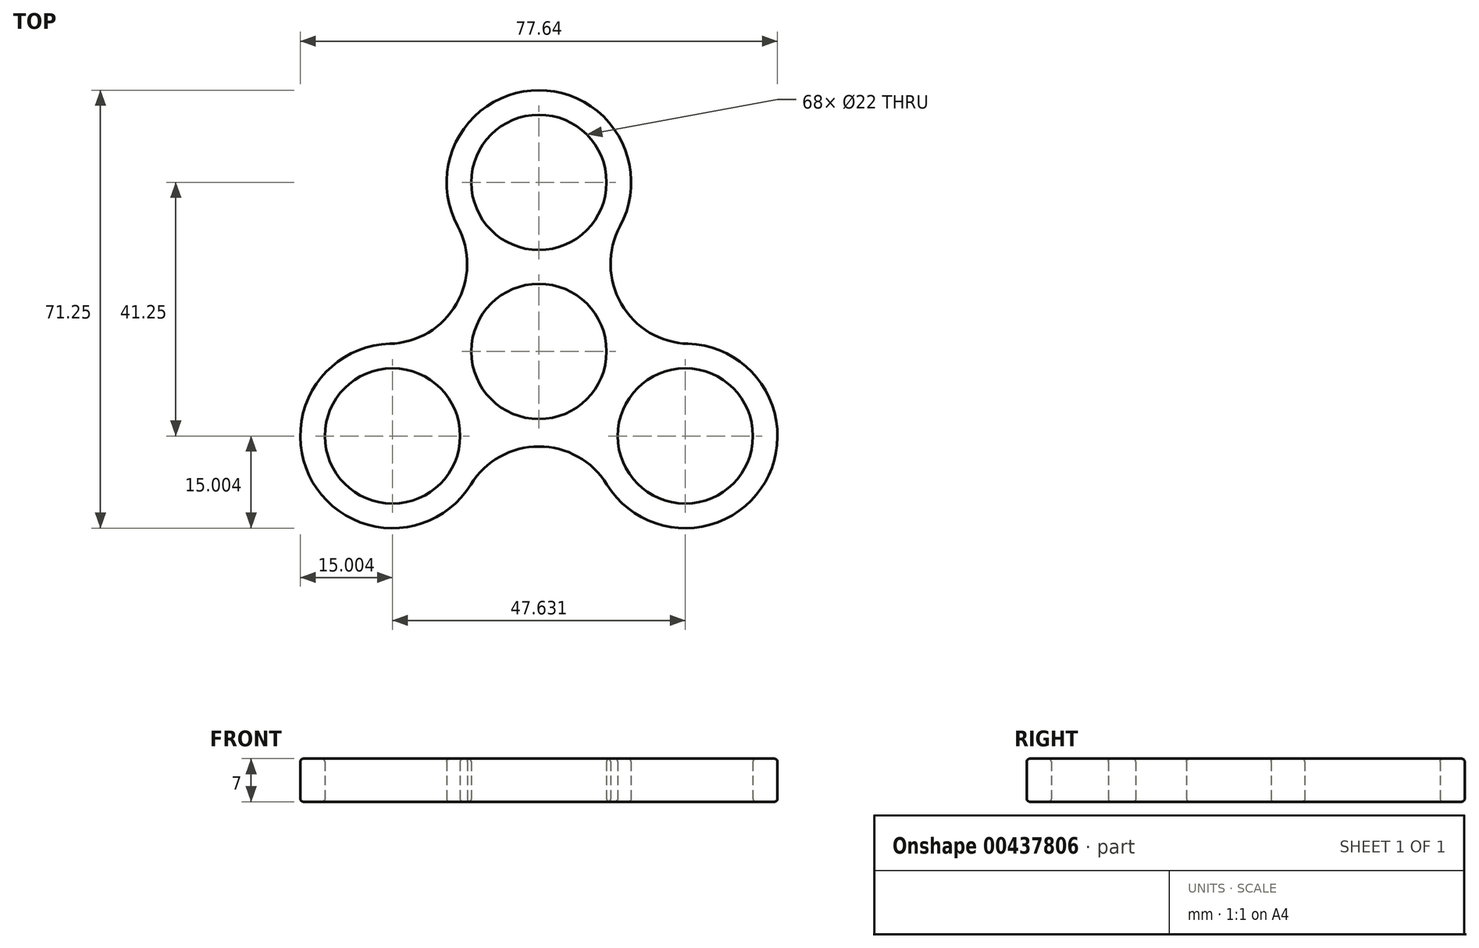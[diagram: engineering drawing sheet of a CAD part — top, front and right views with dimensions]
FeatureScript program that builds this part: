
annotation { "Feature Type Name" : "Feature", "Feature Type Description" : "" }
export const myFeature = defineFeature(function(context is Context, id is Id, definition is map)
    precondition{}
    {
        {
            var Q0;
            Q0=qCreatedBy(makeId("Top.planeOp"),FACE);
            var sketch = newSketch(context, id + "F0", { "sketchPlane" : qUnion([Q0])});
            skLineSegment(sketch, "E0", {"start": v(-74.33, 25.15) * mm, "end": v(-98.15, -16.1) * mm, "construction": true});
            skLineSegment(sketch, "E1", {"start": v(-98.15, -16.1) * mm, "end": v(-50.51, -16.1) * mm, "construction": true});
            skLineSegment(sketch, "E2", {"start": v(-50.51, -16.1) * mm, "end": v(-74.33, 25.15) * mm, "construction": true});
            skLineSegment(sketch, "E3", {"start": v(-74.33, 25.15) * mm, "end": v(-74.33, -16.1) * mm, "construction": true});
            skLineSegment(sketch, "E4", {"start": v(-98.15, -16.1) * mm, "end": v(-62.42, 4.53) * mm, "construction": true});
            skLineSegment(sketch, "E5", {"start": v(-50.51, -16.1) * mm, "end": v(-74.33, -2.35) * mm, "construction": true});
            skCircle(sketch, "E6", {"center": v(-74.33, -2.35) * mm, "radius": 11 * mm});
            skCircle(sketch, "E7", {"center": v(-50.51, -16.1) * mm, "radius": 11 * mm});
            skCircle(sketch, "E8", {"center": v(-98.15, -16.1) * mm, "radius": 11 * mm});
            skCircle(sketch, "E9", {"center": v(-74.33, 25.15) * mm, "radius": 11 * mm});
            skCircle(sketch, "E10", {"center": v(-74.33, 25.15) * mm, "radius": 15 * mm});
            skCircle(sketch, "E11", {"center": v(-50.51, -16.1) * mm, "radius": 15 * mm});
            skCircle(sketch, "E12", {"center": v(-98.15, -16.1) * mm, "radius": 15 * mm});
            skCircle(sketch, "E13", {"center": v(-74.33, -2.35) * mm, "radius": 15 * mm});
            skArc(sketch, "E14", {"start": v(-98.6, -1.1) * mm, "mid": v(-87.73, 5.4) * mm, "end": v(-87.54, 18.05) * mm});
            skArc(sketch, "E15", {"start": v(-61.12, 18.05) * mm, "mid": v(-60.93, 5.4) * mm, "end": v(-50.06, -1.1) * mm});
            skArc(sketch, "E16", {"start": v(-63.27, -23.98) * mm, "mid": v(-74.33, -17.82) * mm, "end": v(-85.39, -23.98) * mm});
            skCircle(sketch, "E17", {"center": v(-74.33, -2.35) * mm, "radius": 42.5 * mm, "construction": true});
            skSolve(sketch);
        }
        {
            var Q0;
            {var subQ6=sQuery(id+"F0.wireOp",EDGE,"E9");Q0=makeQuery(id+"F0.imprint","IMPRINT",FACE,{"disambiguationData":[TD([[makeQuery(id+"F0.imprint","IMPRINT",EDGE,{"derivedFrom":subQ6}),-1.0]])]});}
            var Q1;
            {var subQ0=sQuery(id+"F0.wireOp",EDGE,"E14");var subQ1=sQuery(id+"F0.wireOp",EDGE,"E10");var subQ2=makeQuery(id+"F0.imprint","INTERSECT",VERTEX,{"derivedFrom":[subQ1,subQ0]});Q1=makeQuery(id+"F0.imprint","IMPRINT",FACE,{"disambiguationData":[TD([[makeQuery(id+"F0.imprint","IMPRINT",EDGE,{"disambiguationData":[TD([[subQ2,-1.0]])],"derivedFrom":subQ1}),-1.0]])]});}
            var Q2;
            {var subQ0=sQuery(id+"F0.wireOp",EDGE,"E14");var subQ1=sQuery(id+"F0.wireOp",EDGE,"E12");var subQ2=makeQuery(id+"F0.imprint","INTERSECT",VERTEX,{"derivedFrom":[subQ1,subQ0]});Q2=makeQuery(id+"F0.imprint","IMPRINT",FACE,{"disambiguationData":[TD([[makeQuery(id+"F0.imprint","IMPRINT",EDGE,{"disambiguationData":[TD([[subQ2,1.0]])],"derivedFrom":subQ1}),-1.0]])]});}
            var Q3;
            {var subQ4=sQuery(id+"F0.wireOp",EDGE,"E12");var subQ5=sQuery(id+"F0.wireOp",EDGE,"E6");var subQ6=makeQuery(id+"F0.imprint","INTERSECT",VERTEX,{"derivedFrom":[subQ5,subQ4]});Q3=makeQuery(id+"F0.imprint","IMPRINT",FACE,{"disambiguationData":[TD([[makeQuery(id+"F0.imprint","IMPRINT",EDGE,{"disambiguationData":[TD([[subQ6,1.0]])],"derivedFrom":subQ5}),-1.0]])]});}
            var Q4;
            {var subQ6=sQuery(id+"F0.wireOp",EDGE,"E8");Q4=makeQuery(id+"F0.imprint","IMPRINT",FACE,{"disambiguationData":[TD([[makeQuery(id+"F0.imprint","IMPRINT",EDGE,{"derivedFrom":subQ6}),-1.0]])]});}
            var Q5;
            {var subQ0=sQuery(id+"F0.wireOp",EDGE,"E16");var subQ1=sQuery(id+"F0.wireOp",EDGE,"E12");var subQ2=makeQuery(id+"F0.imprint","INTERSECT",VERTEX,{"derivedFrom":[subQ1,subQ0]});Q5=makeQuery(id+"F0.imprint","IMPRINT",FACE,{"disambiguationData":[TD([[makeQuery(id+"F0.imprint","IMPRINT",EDGE,{"disambiguationData":[TD([[subQ2,-1.0]])],"derivedFrom":subQ1}),-1.0]])]});}
            var Q6;
            {var subQ0=sQuery(id+"F0.wireOp",EDGE,"E16");var subQ1=sQuery(id+"F0.wireOp",EDGE,"E11");var subQ2=makeQuery(id+"F0.imprint","INTERSECT",VERTEX,{"derivedFrom":[subQ1,subQ0]});Q6=makeQuery(id+"F0.imprint","IMPRINT",FACE,{"disambiguationData":[TD([[makeQuery(id+"F0.imprint","IMPRINT",EDGE,{"disambiguationData":[TD([[subQ2,1.0]])],"derivedFrom":subQ1}),-1.0]])]});}
            var Q7;
            {var subQ2=sQuery(id+"F0.wireOp",EDGE,"E12");var subQ5=sQuery(id+"F0.wireOp",EDGE,"E6");var subQ8=makeQuery(id+"F0.imprint","INTERSECT",VERTEX,{"derivedFrom":[subQ5,subQ2]});Q7=makeQuery(id+"F0.imprint","IMPRINT",FACE,{"disambiguationData":[TD([[makeQuery(id+"F0.imprint","IMPRINT",EDGE,{"disambiguationData":[TD([[subQ8,-1.0]])],"derivedFrom":subQ5}),-1.0]])]});}
            var Q8;
            {var subQ2=sQuery(id+"F0.wireOp",EDGE,"E10");var subQ6=sQuery(id+"F0.wireOp",EDGE,"E6");var subQ7=makeQuery(id+"F0.imprint","INTERSECT",VERTEX,{"derivedFrom":[subQ6,subQ2]});Q8=makeQuery(id+"F0.imprint","IMPRINT",FACE,{"disambiguationData":[TD([[makeQuery(id+"F0.imprint","IMPRINT",EDGE,{"disambiguationData":[TD([[subQ7,1.0]])],"derivedFrom":subQ6}),-1.0]])]});}
            var Q9;
            {var subQ0=sQuery(id+"F0.wireOp",EDGE,"E15");var subQ1=sQuery(id+"F0.wireOp",EDGE,"E11");var subQ2=makeQuery(id+"F0.imprint","INTERSECT",VERTEX,{"derivedFrom":[subQ1,subQ0]});Q9=makeQuery(id+"F0.imprint","IMPRINT",FACE,{"disambiguationData":[TD([[makeQuery(id+"F0.imprint","IMPRINT",EDGE,{"disambiguationData":[TD([[subQ2,-1.0]])],"derivedFrom":subQ1}),-1.0]])]});}
            var Q10;
            {var subQ0=sQuery(id+"F0.wireOp",EDGE,"E15");var subQ1=sQuery(id+"F0.wireOp",EDGE,"E10");var subQ2=makeQuery(id+"F0.imprint","INTERSECT",VERTEX,{"derivedFrom":[subQ1,subQ0]});Q10=makeQuery(id+"F0.imprint","IMPRINT",FACE,{"disambiguationData":[TD([[makeQuery(id+"F0.imprint","IMPRINT",EDGE,{"disambiguationData":[TD([[subQ2,1.0]])],"derivedFrom":subQ1}),-1.0]])]});}
            var Q11;
            {var subQ5=sQuery(id+"F0.wireOp",EDGE,"E7");Q11=makeQuery(id+"F0.imprint","IMPRINT",FACE,{"disambiguationData":[TD([[makeQuery(id+"F0.imprint","IMPRINT",EDGE,{"derivedFrom":subQ5}),-1.0]])]});}
            var Q12;
            {var subQ3=sQuery(id+"F0.wireOp",EDGE,"E13");var subQ6=sQuery(id+"F0.wireOp",EDGE,"E9");var subQ7=makeQuery(id+"F0.imprint","INTERSECT",VERTEX,{"disambiguationData":[OD(0.0)],"derivedFrom":[subQ6,subQ3]});Q12=makeQuery(id+"F0.imprint","IMPRINT",FACE,{"disambiguationData":[TD([[makeQuery(id+"F0.imprint","IMPRINT",EDGE,{"disambiguationData":[TD([[subQ7,1.0]])],"derivedFrom":subQ6}),-1.0]])]});}
            var Q13;
            {var subQ2=sQuery(id+"F0.wireOp",EDGE,"E13");var subQ6=sQuery(id+"F0.wireOp",EDGE,"E8");var subQ8=makeQuery(id+"F0.imprint","INTERSECT",VERTEX,{"disambiguationData":[OD(0.0)],"derivedFrom":[subQ6,subQ2]});Q13=makeQuery(id+"F0.imprint","IMPRINT",FACE,{"disambiguationData":[TD([[makeQuery(id+"F0.imprint","IMPRINT",EDGE,{"disambiguationData":[TD([[subQ8,-1.0]])],"derivedFrom":subQ6}),-1.0]])]});}
            var Q14;
            {var subQ2=sQuery(id+"F0.wireOp",EDGE,"E13");var subQ6=sQuery(id+"F0.wireOp",EDGE,"E7");var subQ7=makeQuery(id+"F0.imprint","INTERSECT",VERTEX,{"disambiguationData":[OD(0.0)],"derivedFrom":[subQ6,subQ2]});Q14=makeQuery(id+"F0.imprint","IMPRINT",FACE,{"disambiguationData":[TD([[makeQuery(id+"F0.imprint","IMPRINT",EDGE,{"disambiguationData":[TD([[subQ7,1.0]])],"derivedFrom":subQ6}),-1.0]])]});}
            var Q15;
            {var subQ0=sQuery(id+"F0.wireOp",EDGE,"E13");var subQ1=sQuery(id+"F0.wireOp",EDGE,"E10");var subQ2=makeQuery(id+"F0.imprint","INTERSECT",VERTEX,{"disambiguationData":[OD(0.0)],"derivedFrom":[subQ1,subQ0]});Q15=makeQuery(id+"F0.imprint","IMPRINT",FACE,{"disambiguationData":[TD([[makeQuery(id+"F0.imprint","IMPRINT",EDGE,{"disambiguationData":[TD([[subQ2,-1.0]])],"derivedFrom":subQ1}),1.0]])]});}
            var Q16;
            {var subQ0=sQuery(id+"F0.wireOp",EDGE,"E13");var subQ1=sQuery(id+"F0.wireOp",EDGE,"E11");var subQ2=makeQuery(id+"F0.imprint","INTERSECT",VERTEX,{"disambiguationData":[OD(0.0)],"derivedFrom":[subQ1,subQ0]});Q16=makeQuery(id+"F0.imprint","IMPRINT",FACE,{"disambiguationData":[TD([[makeQuery(id+"F0.imprint","IMPRINT",EDGE,{"disambiguationData":[TD([[subQ2,-1.0]])],"derivedFrom":subQ1}),1.0]])]});}
            var Q17;
            {var subQ0=sQuery(id+"F0.wireOp",EDGE,"E13");var subQ1=sQuery(id+"F0.wireOp",EDGE,"E12");var subQ2=makeQuery(id+"F0.imprint","INTERSECT",VERTEX,{"disambiguationData":[OD(0.0)],"derivedFrom":[subQ1,subQ0]});Q17=makeQuery(id+"F0.imprint","IMPRINT",FACE,{"disambiguationData":[TD([[makeQuery(id+"F0.imprint","IMPRINT",EDGE,{"disambiguationData":[TD([[subQ2,1.0]])],"derivedFrom":subQ1}),1.0]])]});}
            extrude(context, id + "F1", {"entities" : qUnion([Q0, Q1, Q2, Q3, Q4, Q5, Q6, Q7, Q8, Q9, Q10, Q11, Q12, Q13, Q14, Q15, Q16, Q17]), "depth" : 7 * mm, "offsetDistance" : 25 * mm});
        }
        {
            var Q0;
            Q0=makeQuery(id+"F1.opExtrude","CAP_FACE",FACE,{"disambiguationData":[OSD([sQuery(id+"F0.wireOp",EDGE,"E6"),sQuery(id+"F0.wireOp",EDGE,"E7"),sQuery(id+"F0.wireOp",EDGE,"E8"),sQuery(id+"F0.wireOp",EDGE,"E9"),sQuery(id+"F0.wireOp",EDGE,"E10"),sQuery(id+"F0.wireOp",EDGE,"E11"),sQuery(id+"F0.wireOp",EDGE,"E12"),sQuery(id+"F0.wireOp",EDGE,"E14"),sQuery(id+"F0.wireOp",EDGE,"E15"),sQuery(id+"F0.wireOp",EDGE,"E16")])],"isStart":true});
            var Q1;
            Q1=makeQuery(id+"F1.opExtrude","CAP_FACE",FACE,{"disambiguationData":[OSD([sQuery(id+"F0.wireOp",EDGE,"E6"),sQuery(id+"F0.wireOp",EDGE,"E7"),sQuery(id+"F0.wireOp",EDGE,"E8"),sQuery(id+"F0.wireOp",EDGE,"E9"),sQuery(id+"F0.wireOp",EDGE,"E10"),sQuery(id+"F0.wireOp",EDGE,"E11"),sQuery(id+"F0.wireOp",EDGE,"E12"),sQuery(id+"F0.wireOp",EDGE,"E14"),sQuery(id+"F0.wireOp",EDGE,"E15"),sQuery(id+"F0.wireOp",EDGE,"E16")])],"isStart":false});
            fillet(context, id + "F2", {"entities" : qUnion([Q0, Q1]), "radius" : 0.5 * mm, "tangentPropagation" : true, "allowEdgeOverflow" : false});
        }
    });
